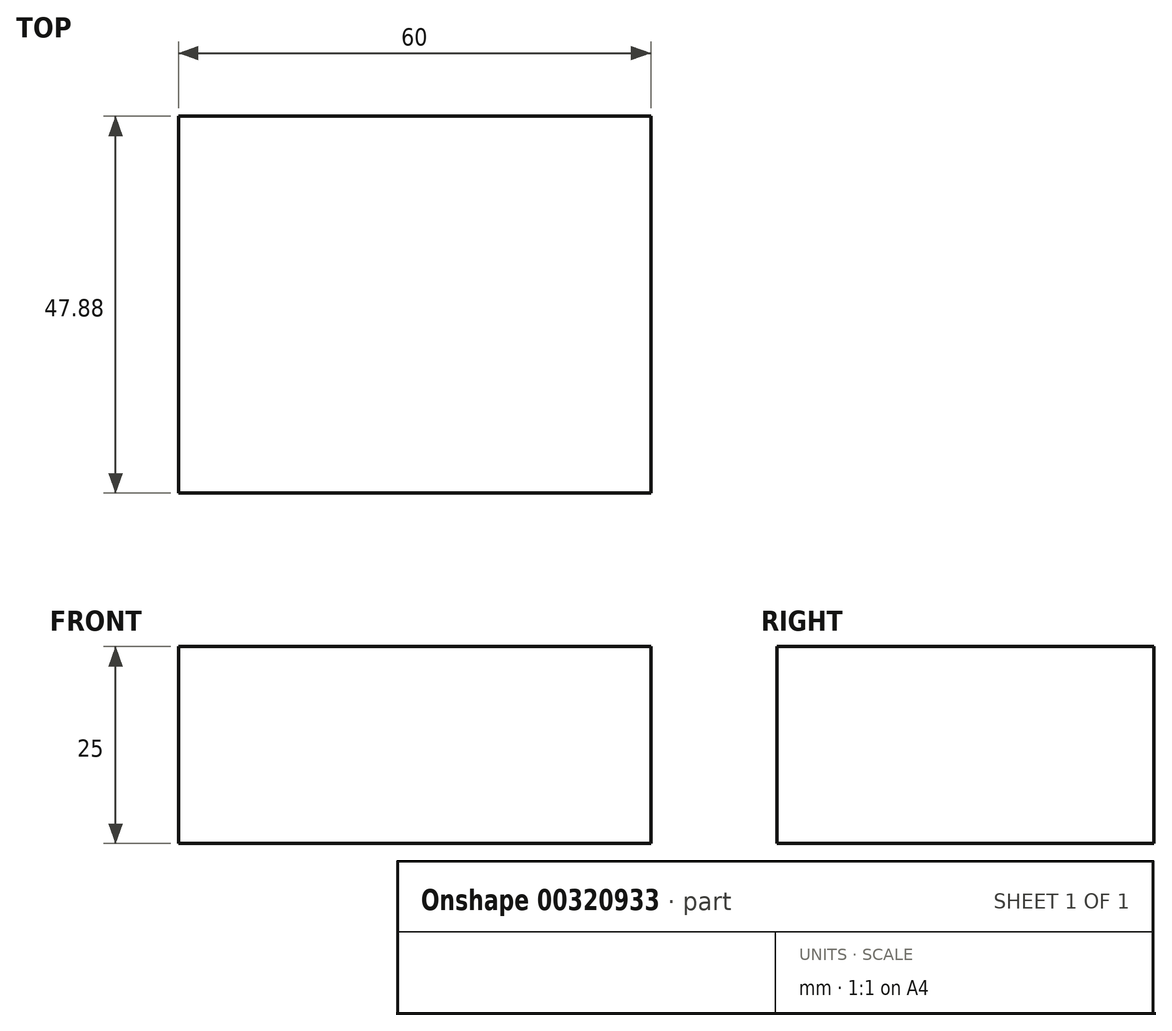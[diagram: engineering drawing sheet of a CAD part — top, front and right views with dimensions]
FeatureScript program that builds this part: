
annotation { "Feature Type Name" : "Feature", "Feature Type Description" : "" }
export const myFeature = defineFeature(function(context is Context, id is Id, definition is map)
    precondition{}
    {
        {
            var Q0;
            Q0=qCreatedBy(makeId("Top.planeOp"),FACE);
            var sketch = newSketch(context, id + "F0", { "sketchPlane" : qUnion([Q0])});
            skLineSegment(sketch, "E0.bottom", {"start": v(30, 23.94) * mm, "end": v(-30, 23.94) * mm});
            skLineSegment(sketch, "E0.top", {"start": v(30, -23.94) * mm, "end": v(-30, -23.94) * mm});
            skLineSegment(sketch, "E0.left", {"start": v(30, 23.94) * mm, "end": v(30, -23.94) * mm});
            skLineSegment(sketch, "E0.right", {"start": v(-30, 23.94) * mm, "end": v(-30, -23.94) * mm});
            skPoint(sketch, "E0.middle", {"position": v(0, 0) * mm});
            skEllipse(sketch, "E1", {"center": v(-81.55, 39.13) * mm, "majorRadius": 42.5 * mm, "minorRadius": 21.31 * mm, "majorAxis": v(-0.25, -0.97)});
            skSolve(sketch);
        }
        {
            var Q0;
            Q0=makeQuery(id+"F0.imprint","IMPRINT",FACE,{"disambiguationData":[TD([[makeQuery(id+"F0.imprint","IMPRINT",EDGE,{"derivedFrom":sQuery(id+"F0.wireOp",EDGE,"E0.bottom")}),1.0]])]});
            extrude(context, id + "F1", {"entities" : qUnion([Q0]), "depth" : 25 * mm});
        }
    });
